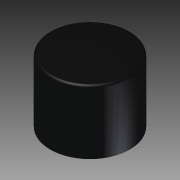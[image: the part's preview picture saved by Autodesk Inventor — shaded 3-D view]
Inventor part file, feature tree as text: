
AUTODESK INVENTOR PART (.ipt)
format: ipt  version: 2015 (Build 190159000, 159)  size: 94,720 bytes
history: native  units: in
note: dims shown in document units (in); Inventor stores cm internally (conversion verified against a paired STEP export)
features: other x7, revolve x1, sketch x1
ambient origin geometry x8: Origin, YZ Plane, XZ Plane, XY Plane, X Axis, Y Axis, Z Axis, Center Point
bodies: Solid1 (feature_tree)
feature tree (9):
  revolve  "Revolution1"  [1 undecoded]
  other  "to_plunger_XY"
  other  "to_plunger_YZ"
  other  "to_plunger_ZX"
  other  "to_plunger_X"
  other  "to_plunger_Y"
  other  "to_plunger_Z"
  other  "to_plunger_Center"
  sketch  "Sketch_3"  dims[d0=360.0deg]
note: 1 required parameter value undecoded (feature->parameter linkage not recoverable at this tier; creation-order binding heuristic only, values carry confidence <= 0.55)
